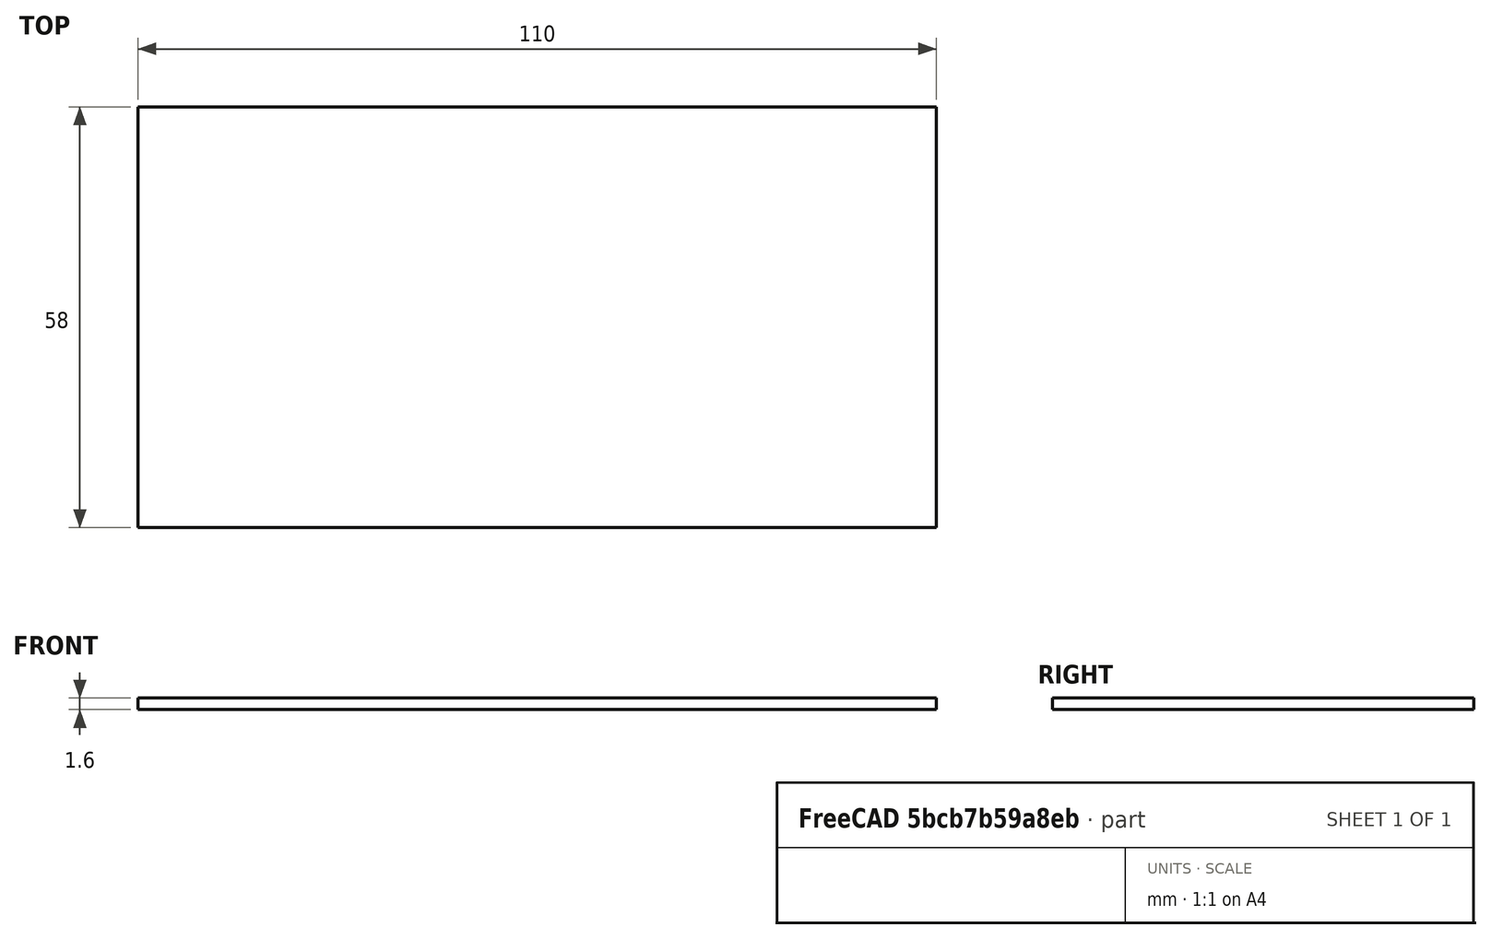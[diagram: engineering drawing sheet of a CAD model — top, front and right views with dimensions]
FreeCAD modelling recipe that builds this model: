
FCSTD DOCUMENT  (FreeCAD 0.19R24276 (Git))
Label: pir-baffel-top
License: All rights reserved
LicenseURL: http://en.wikipedia.org/wiki/All_rights_reserved
objects: Sketcher::SketchObject×1, PartDesign::Pad×1, PartDesign::CoordinateSystem×1, PartDesign::Body×1
note: 5 computed .brp shape members not serialized (recipe doc carries the construction recipe); baked Part::Feature solids carry a one-line shape summary decoded from their .brp

FEATURE [Sketcher::SketchObject] Sketch
  FullyConstrained = true
  MapMode = 5
  Support = -> [XY_Plane]
  sketch-geometry (4):
    g0: LineSegment StartX=-55 StartY=29 StartZ=0 EndX=55 EndY=29 EndZ=0
    g1: LineSegment StartX=55 StartY=29 StartZ=0 EndX=55 EndY=-29 EndZ=0
    g2: LineSegment StartX=55 StartY=-29 StartZ=0 EndX=-55 EndY=-29 EndZ=0
    g3: LineSegment StartX=-55 StartY=-29 StartZ=0 EndX=-55 EndY=29 EndZ=0
  constraints (10):
    c: Coincident(g0,g1)
    c: Coincident(g1,g2)
    c: Coincident(g2,g3)
    c: Coincident(g3,g0)
    c: Horizontal(g2)
    c: Vertical(g1)
    c: DistanceX(g0,g0) = 110
    c: DistanceY(g3,g3) = 58
    c: Symmetric(g0,g0,g-2)
    c: Symmetric(g0,g2,g-1)
FEATURE [PartDesign::Pad] Pad
  Direction = (1,1,1)
  Length = 1.6
  Length2 = 100
  Profile = -> Sketch
  Type = 0
FEATURE [PartDesign::CoordinateSystem] LCS_top
  AttacherType = Attacher::AttachEngine3D
  MapMode = 45
  Placement = pos=(0,0,0.8) rot=(0,0,1;1.5708rad)
  Support = -> [Pad]
FEATURE [PartDesign::Body] Body
  Group = -> [Sketch,Pad,LCS_top]
  Origin = -> Origin
  Tip = -> Pad
